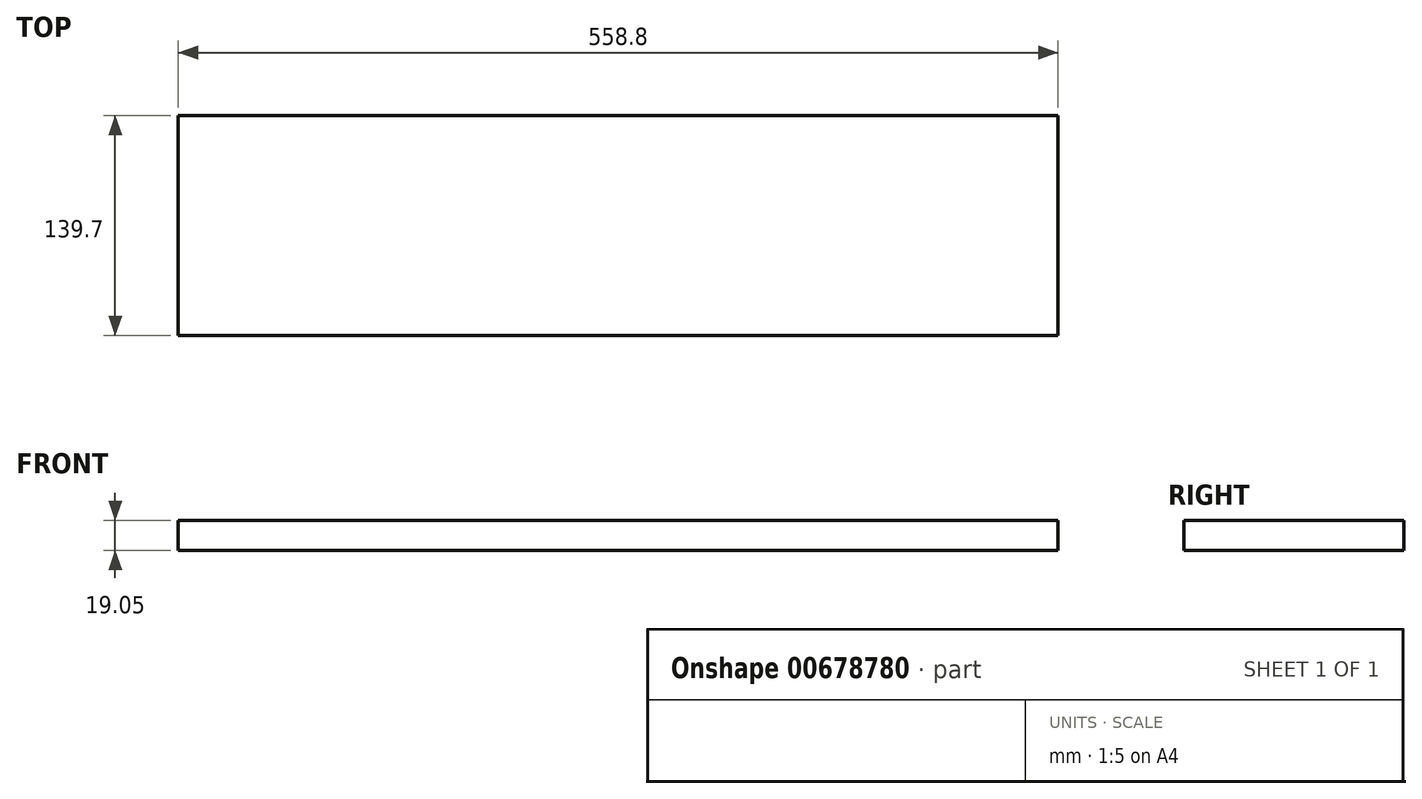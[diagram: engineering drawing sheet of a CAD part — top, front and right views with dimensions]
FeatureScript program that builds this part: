
annotation { "Feature Type Name" : "Feature", "Feature Type Description" : "" }
export const myFeature = defineFeature(function(context is Context, id is Id, definition is map)
    precondition{}
    {
        {
            var Q0;
            Q0=qCreatedBy(makeId("Top.planeOp"),FACE);
            var sketch = newSketch(context, id + "F0", { "sketchPlane" : qUnion([Q0])});
            skLineSegment(sketch, "E0.bottom", {"start": v(-342.92, 108.7) * mm, "end": v(215.88, 108.7) * mm});
            skLineSegment(sketch, "E0.top", {"start": v(-342.92, -31) * mm, "end": v(215.88, -31) * mm});
            skLineSegment(sketch, "E0.left", {"start": v(-342.92, 108.7) * mm, "end": v(-342.92, -31) * mm});
            skLineSegment(sketch, "E0.right", {"start": v(215.88, 108.7) * mm, "end": v(215.88, -31) * mm});
            skSolve(sketch);
        }
        {
            var Q0;
            Q0=makeQuery(id+"F0.imprint","IMPRINT",FACE,{"disambiguationData":[TD([[makeQuery(id+"F0.imprint","IMPRINT",EDGE,{"derivedFrom":sQuery(id+"F0.wireOp",EDGE,"E0.bottom")}),-1.0]])]});
            extrude(context, id + "F1", {"entities" : qUnion([Q0]), "depth" : 19.05 * mm, "offsetDistance" : 25.4 * mm});
        }
    });
